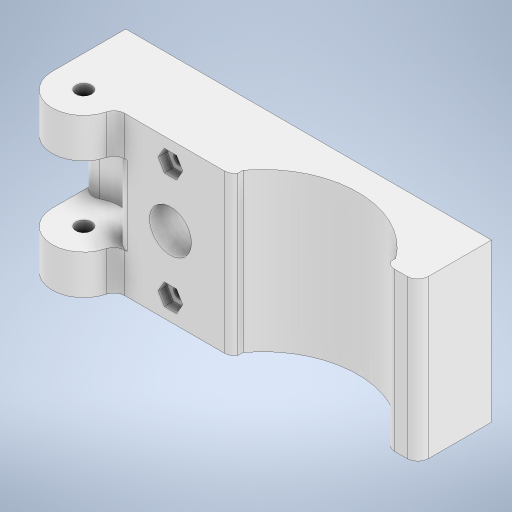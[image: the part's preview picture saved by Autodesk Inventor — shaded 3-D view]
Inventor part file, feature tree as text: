
AUTODESK INVENTOR PART (.ipt)
format: ipt  version: 2023 (Build 270158000, 158)  size: 332,800 bytes
history: native  units: mm
features: extrude x7, sketch x4, fillet x1
ambient origin geometry x8: Origin, YZ Plane, XZ Plane, XY Plane, X Axis, Y Axis, Z Axis, Center Point
bodies: Solid1 (feature_tree)
feature tree (12):
  sketch  "Sketch2"  dims[d3=2.0mm d17=3.0mm]
  extrude  "Extrusion1"  Depth=2.0mm
  extrude  "Extrusion2"  Depth=30.0mm TaperAngle=0.0deg
  extrude  "Extrusion10"  Depth=15.0mm
  fillet  "Fillet4"  Radius=1.0mm
  extrude  "Extrusion15"  Depth=2.0mm
  sketch  "Sketch17"  dims[d18=2.0mm d26=30.0mm d27=0.0mm]
  extrude  "Extrusion23"  Depth=1.7mm
  sketch  "Sketch20"  dims[d62=10.0mm d63=0.0mm d95=2.0mm d99=8.0mm d101=15.0mm d102=0.0mm d106=47.0mm d131=11.0mm d132=15.0mm d137=2.199496mm d140=12.0mm d141=69.5mm d142=14.0mm d143=6.0mm d144=17.5mm d145=19.0mm d146=5.4mm d147=6.225mm d148=13.4mm d156=11.2mm d157=4.5mm d158=0.0mm d159=2.2mm d160=11.0mm d163=4.05mm d164=10.0mm d165=0.0mm d166=1.7mm d167=0.0mm d45=0.0mm d46=0.0mm d47=0.0mm d48=0.0mm d52=0.0mm d53=0.0mm d54=0.0mm d55=0.0mm d67=0.5mm d68=0.872665mm d69=0.5mm d70=0.872665mm d122=0.5mm d123=0.872665mm d124=0.5mm d125=0.872665mm]
  extrude  "Extrusion24"  Depth=15.0mm TaperAngle=0.0deg
  extrude  "Extrusion25"  Depth=1.7mm
  sketch  "Sketch19"  dims[d28=15.0mm d29=0.0mm d59=1.0mm d60=1.0mm]
